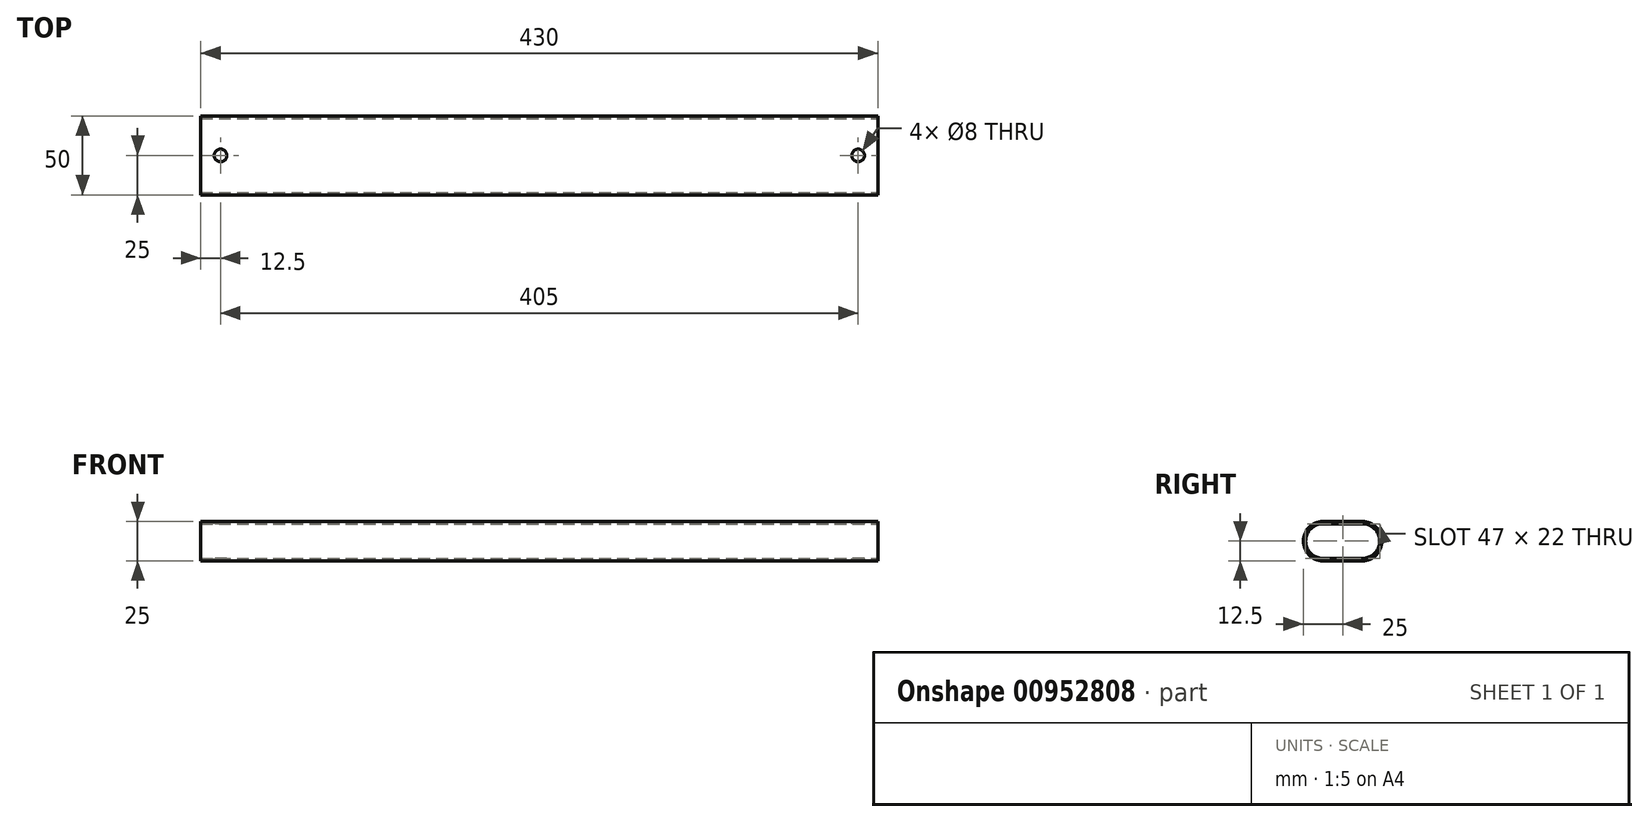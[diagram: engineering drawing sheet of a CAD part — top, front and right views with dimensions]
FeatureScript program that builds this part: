
annotation { "Feature Type Name" : "Feature", "Feature Type Description" : "" }
export const myFeature = defineFeature(function(context is Context, id is Id, definition is map)
    precondition{}
    {
        {
            var Q0;
            Q0=qCreatedBy(makeId("Right.planeOp"),FACE);
            var sketch = newSketch(context, id + "F0", { "sketchPlane" : qUnion([Q0])});
            skLineSegment(sketch, "E0.bottom", {"start": v(-12.5, 12.5) * mm, "end": v(12.5, 12.5) * mm});
            skLineSegment(sketch, "E0.top", {"start": v(-12.5, -12.5) * mm, "end": v(12.5, -12.5) * mm});
            skLineSegment(sketch, "E0.left", {"start": v(-25, 0) * mm, "end": v(-25, 0) * mm});
            skLineSegment(sketch, "E0.right", {"start": v(25, 0) * mm, "end": v(25, 0) * mm});
            skPoint(sketch, "E0.middle", {"position": v(0, 0) * mm});
            skPoint(sketch, "E1.visualSharp", {"position": v(-25, 12.5) * mm});
            skArc(sketch, "E1.filletArc", {"start": v(-12.5, 12.5) * mm, "mid": v(-21.34, 8.84) * mm, "end": v(-25, 0) * mm});
            skPoint(sketch, "E2.visualSharp", {"position": v(-25, -12.5) * mm});
            skArc(sketch, "E2.filletArc", {"start": v(-25, 0) * mm, "mid": v(-21.34, -8.84) * mm, "end": v(-12.5, -12.5) * mm});
            skPoint(sketch, "E3.visualSharp", {"position": v(25, -12.5) * mm});
            skArc(sketch, "E3.filletArc", {"start": v(12.5, -12.5) * mm, "mid": v(21.34, -8.84) * mm, "end": v(25, 0) * mm});
            skPoint(sketch, "E4.visualSharp", {"position": v(25, 12.5) * mm});
            skArc(sketch, "E4.filletArc", {"start": v(25, 0) * mm, "mid": v(21.34, 8.84) * mm, "end": v(12.5, 12.5) * mm});
            skLineSegment(sketch, "E5.bottom", {"start": v(12.5, 11) * mm, "end": v(-12.5, 11) * mm});
            skLineSegment(sketch, "E5.top", {"start": v(12.5, -11) * mm, "end": v(-12.5, -11) * mm});
            skLineSegment(sketch, "E5.left", {"start": v(23.5, 0) * mm, "end": v(23.5, 0) * mm});
            skLineSegment(sketch, "E5.right", {"start": v(-23.5, 0) * mm, "end": v(-23.5, 0) * mm});
            skPoint(sketch, "E6.visualSharp", {"position": v(-23.5, 11) * mm});
            skArc(sketch, "E6.filletArc", {"start": v(-12.5, 11) * mm, "mid": v(-20.28, 7.78) * mm, "end": v(-23.5, 0) * mm});
            skPoint(sketch, "E7.visualSharp", {"position": v(-23.5, -11) * mm});
            skArc(sketch, "E7.filletArc", {"start": v(-23.5, 0) * mm, "mid": v(-20.28, -7.78) * mm, "end": v(-12.5, -11) * mm});
            skPoint(sketch, "E8.visualSharp", {"position": v(23.5, -11) * mm});
            skArc(sketch, "E8.filletArc", {"start": v(12.5, -11) * mm, "mid": v(20.28, -7.78) * mm, "end": v(23.5, 0) * mm});
            skPoint(sketch, "E9.visualSharp", {"position": v(23.5, 11) * mm});
            skArc(sketch, "E9.filletArc", {"start": v(23.5, 0) * mm, "mid": v(20.28, 7.78) * mm, "end": v(12.5, 11) * mm});
            skSolve(sketch);
        }
        {
            var Q0;
            Q0 = qSketchRegion(id + "F0", true);
            extrude(context, id + "F1", {"entities" : qUnion([Q0]), "oppositeDirection" : true, "depth" : 430 * mm, "offsetDistance" : 25 * mm});
        }
        {
            var Q0;
            Q0=makeQuery(id+"F1.opExtrude","SWEPT_FACE",FACE,{"disambiguationData":[OSD([sQuery(id+"F0.wireOp",EDGE,"E0.bottom")])]});
            var sketch = newSketch(context, id + "F2", { "sketchPlane" : qUnion([Q0])});
            skLineSegment(sketch, "E10", {"start": v(0, 0) * mm, "end": v(-12.5, 0) * mm, "construction": true});
            skCircle(sketch, "E11", {"center": v(-12.5, 0) * mm, "radius": 4 * mm});
            skLineSegment(sketch, "E12", {"start": v(-430, 0) * mm, "end": v(-417.5, 0) * mm, "construction": true});
            skCircle(sketch, "E13", {"center": v(-417.5, 0) * mm, "radius": 4 * mm});
            skSolve(sketch);
        }
        {
            var Q0;
            Q0 = qSketchRegion(id + "F2", true);
            extrude(context, id + "F3", {"entities" : qUnion([Q0]), "operationType" : NewBodyOperationType.REMOVE, "oppositeDirection" : true, "depth" : 30 * mm, "offsetDistance" : 25 * mm});
        }
    });
